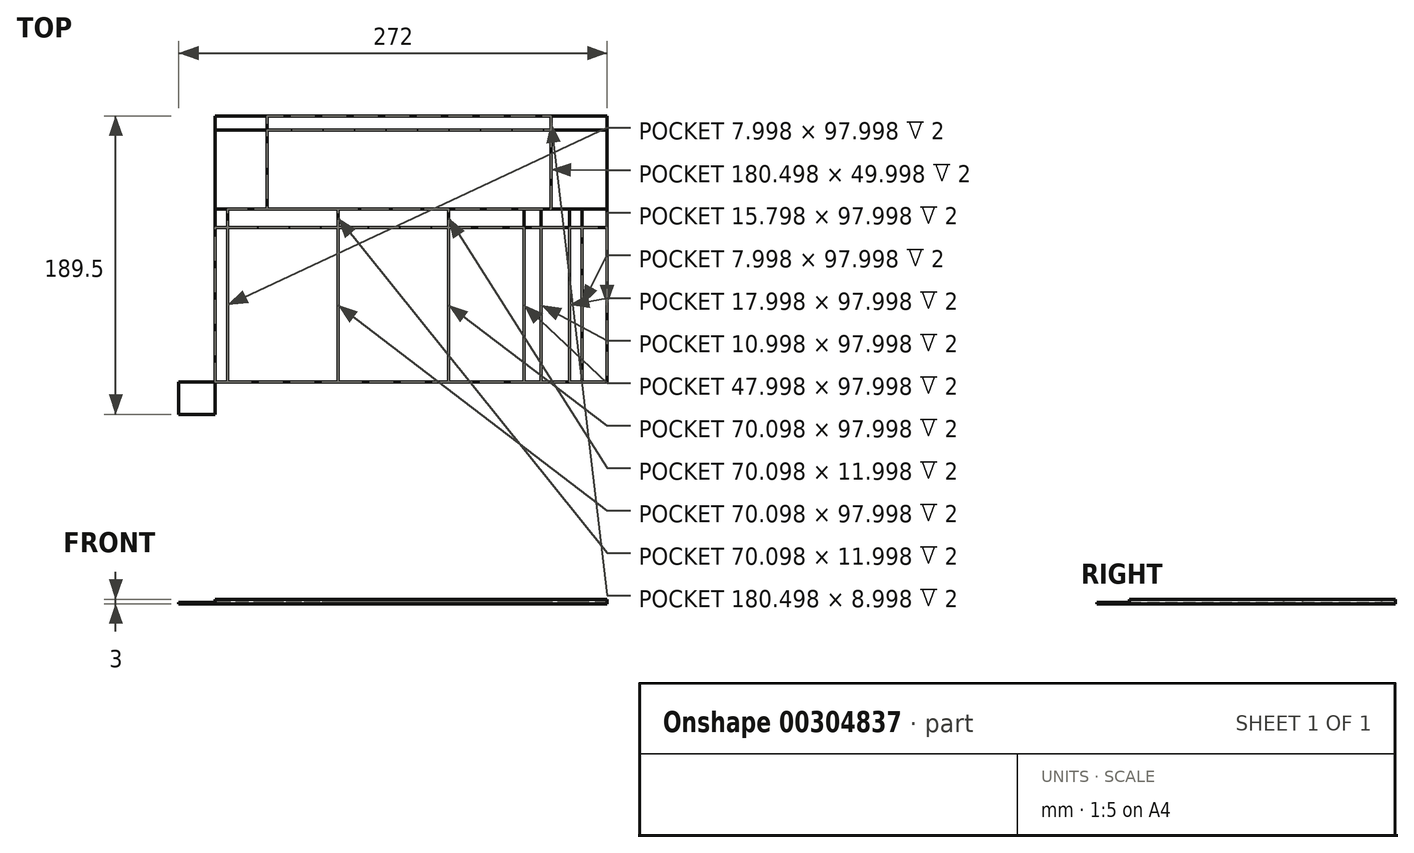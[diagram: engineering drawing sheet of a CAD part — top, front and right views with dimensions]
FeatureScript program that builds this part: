
annotation { "Feature Type Name" : "Feature", "Feature Type Description" : "" }
export const myFeature = defineFeature(function(context is Context, id is Id, definition is map)
    precondition{}
    {
        {
            var Q0;
            Q0=qCreatedBy(makeId("Top.planeOp"),FACE);
            var sketch = newSketch(context, id + "F0", { "sketchPlane" : qUnion([Q0])});
            skLineSegment(sketch, "E0.bottom", {"start": v(0, 0) * mm, "end": v(290, 0) * mm, "construction": true});
            skLineSegment(sketch, "E0.top", {"start": v(0, 210) * mm, "end": v(290, 210) * mm, "construction": true});
            skLineSegment(sketch, "E0.left", {"start": v(0, 0) * mm, "end": v(0, 210) * mm, "construction": true});
            skLineSegment(sketch, "E0.right", {"start": v(290, 0) * mm, "end": v(290, 210) * mm, "construction": true});
            skLineSegment(sketch, "E1.0", {"start": v(20.5, 189.5) * mm, "end": v(269.5, 189.5) * mm});
            skLineSegment(sketch, "E1.1", {"start": v(20.5, 20.5) * mm, "end": v(20.5, 189.5) * mm});
            skLineSegment(sketch, "E1.2", {"start": v(20.5, 20.5) * mm, "end": v(269.5, 20.5) * mm});
            skLineSegment(sketch, "E1.3", {"start": v(269.5, 20.5) * mm, "end": v(269.5, 189.5) * mm});
            skSolve(sketch);
        }
        {
            var Q0;
            Q0=qCreatedBy(makeId("Top.planeOp"),FACE);
            var sketch = newSketch(context, id + "F1", { "sketchPlane" : qUnion([Q0])});
            skLineSegment(sketch, "E2.bottom", {"start": v(20.5, 189.5) * mm, "end": v(53.5, 189.5) * mm});
            skLineSegment(sketch, "E2.top", {"start": v(20.5, 180.5) * mm, "end": v(53.5, 180.5) * mm});
            skLineSegment(sketch, "E2.left", {"start": v(20.5, 189.5) * mm, "end": v(20.5, 180.5) * mm});
            skLineSegment(sketch, "E2.right", {"start": v(53.5, 189.5) * mm, "end": v(53.5, 180.5) * mm});
            skLineSegment(sketch, "E3.bottom", {"start": v(53.5, 189.5) * mm, "end": v(234, 189.5) * mm});
            skLineSegment(sketch, "E3.top", {"start": v(53.5, 180.5) * mm, "end": v(234, 180.5) * mm});
            skLineSegment(sketch, "E3.right", {"start": v(234, 189.5) * mm, "end": v(234, 180.5) * mm});
            skLineSegment(sketch, "E4.bottom", {"start": v(234, 189.5) * mm, "end": v(269.5, 189.5) * mm});
            skLineSegment(sketch, "E4.top", {"start": v(234, 180.5) * mm, "end": v(269.5, 180.5) * mm});
            skLineSegment(sketch, "E4.right", {"start": v(269.5, 189.5) * mm, "end": v(269.5, 180.5) * mm});
            skLineSegment(sketch, "E5.top", {"start": v(20.5, 130.5) * mm, "end": v(53.5, 130.5) * mm});
            skLineSegment(sketch, "E5.left", {"start": v(20.5, 180.5) * mm, "end": v(20.5, 130.5) * mm});
            skLineSegment(sketch, "E5.right", {"start": v(53.5, 180.5) * mm, "end": v(53.5, 130.5) * mm});
            skLineSegment(sketch, "E6.top", {"start": v(53.5, 130.5) * mm, "end": v(234, 130.5) * mm});
            skLineSegment(sketch, "E6.right", {"start": v(234, 180.5) * mm, "end": v(234, 130.5) * mm});
            skLineSegment(sketch, "E7.top", {"start": v(234, 130.5) * mm, "end": v(269.5, 130.5) * mm});
            skLineSegment(sketch, "E7.right", {"start": v(269.5, 180.5) * mm, "end": v(269.5, 130.5) * mm});
            skLineSegment(sketch, "E8.bottom", {"start": v(20.5, 180.5) * mm, "end": v(269.5, 180.5) * mm});
            skLineSegment(sketch, "E8.top", {"start": v(20.5, 189.5) * mm, "end": v(269.5, 189.5) * mm});
            skLineSegment(sketch, "E8.left", {"start": v(20.5, 180.5) * mm, "end": v(20.5, 189.5) * mm});
            skLineSegment(sketch, "E8.right", {"start": v(269.5, 180.5) * mm, "end": v(269.5, 189.5) * mm});
            skLineSegment(sketch, "E9.bottom", {"start": v(20.5, 130.5) * mm, "end": v(28.5, 130.5) * mm});
            skLineSegment(sketch, "E9.top", {"start": v(20.5, 118.5) * mm, "end": v(28.5, 118.5) * mm, "construction": true});
            skLineSegment(sketch, "E9.left", {"start": v(20.5, 130.5) * mm, "end": v(20.5, 118.5) * mm});
            skLineSegment(sketch, "E9.right", {"start": v(28.5, 130.5) * mm, "end": v(28.5, 118.5) * mm, "construction": true});
            skLineSegment(sketch, "E10.2", {"start": v(20.5, 118.5) * mm, "end": v(28.5, 118.5) * mm});
            skLineSegment(sketch, "E10.3", {"start": v(28.5, 130.5) * mm, "end": v(28.5, 118.5) * mm});
            skLineSegment(sketch, "E11.top", {"start": v(20.5, 20.5) * mm, "end": v(28.5, 20.5) * mm});
            skLineSegment(sketch, "E11.left", {"start": v(20.5, 118.5) * mm, "end": v(20.5, 20.5) * mm});
            skLineSegment(sketch, "E11.right", {"start": v(28.5, 118.5) * mm, "end": v(28.5, 20.5) * mm, "construction": true});
            skLineSegment(sketch, "E12.3", {"start": v(28.5, 118.5) * mm, "end": v(28.5, 20.5) * mm});
            skLineSegment(sketch, "E13.bottom", {"start": v(28.5, 130.5) * mm, "end": v(98.6, 130.5) * mm});
            skLineSegment(sketch, "E13.top", {"start": v(28.5, 118.5) * mm, "end": v(98.6, 118.5) * mm, "construction": true});
            skLineSegment(sketch, "E13.right", {"start": v(98.6, 130.5) * mm, "end": v(98.6, 118.5) * mm, "construction": true});
            skLineSegment(sketch, "E14.2", {"start": v(28.5, 118.5) * mm, "end": v(98.6, 118.5) * mm});
            skLineSegment(sketch, "E14.3", {"start": v(98.6, 130.5) * mm, "end": v(98.6, 118.5) * mm});
            skLineSegment(sketch, "E15.top", {"start": v(28.5, 20.5) * mm, "end": v(98.6, 20.5) * mm});
            skLineSegment(sketch, "E15.right", {"start": v(98.6, 118.5) * mm, "end": v(98.6, 20.5) * mm, "construction": true});
            skLineSegment(sketch, "E16.3", {"start": v(98.6, 118.5) * mm, "end": v(98.6, 20.5) * mm});
            skLineSegment(sketch, "E17.bottom", {"start": v(98.6, 130.5) * mm, "end": v(168.7, 130.5) * mm, "construction": true});
            skLineSegment(sketch, "E17.top", {"start": v(98.6, 118.5) * mm, "end": v(168.7, 118.5) * mm, "construction": true});
            skLineSegment(sketch, "E17.right", {"start": v(168.7, 130.5) * mm, "end": v(168.7, 118.5) * mm, "construction": true});
            skLineSegment(sketch, "E18.0", {"start": v(98.6, 130.5) * mm, "end": v(168.7, 130.5) * mm});
            skLineSegment(sketch, "E18.2", {"start": v(98.6, 118.5) * mm, "end": v(168.7, 118.5) * mm});
            skLineSegment(sketch, "E18.3", {"start": v(168.7, 130.5) * mm, "end": v(168.7, 118.5) * mm});
            skLineSegment(sketch, "E19.top", {"start": v(98.6, 20.5) * mm, "end": v(168.7, 20.5) * mm, "construction": true});
            skLineSegment(sketch, "E19.right", {"start": v(168.7, 118.5) * mm, "end": v(168.7, 20.5) * mm, "construction": true});
            skLineSegment(sketch, "E20.2", {"start": v(98.6, 20.5) * mm, "end": v(168.7, 20.5) * mm});
            skLineSegment(sketch, "E20.3", {"start": v(168.7, 118.5) * mm, "end": v(168.7, 20.5) * mm});
            skLineSegment(sketch, "E21.bottom", {"start": v(168.7, 130.5) * mm, "end": v(216.7, 130.5) * mm, "construction": true});
            skLineSegment(sketch, "E21.top", {"start": v(168.7, 118.5) * mm, "end": v(216.7, 118.5) * mm, "construction": true});
            skLineSegment(sketch, "E21.right", {"start": v(216.7, 130.5) * mm, "end": v(216.7, 118.5) * mm, "construction": true});
            skLineSegment(sketch, "E22.0", {"start": v(168.7, 130.5) * mm, "end": v(216.7, 130.5) * mm});
            skLineSegment(sketch, "E22.2", {"start": v(168.7, 118.5) * mm, "end": v(216.7, 118.5) * mm});
            skLineSegment(sketch, "E22.3", {"start": v(216.7, 130.5) * mm, "end": v(216.7, 118.5) * mm});
            skLineSegment(sketch, "E23.top", {"start": v(168.7, 20.5) * mm, "end": v(216.7, 20.5) * mm, "construction": true});
            skLineSegment(sketch, "E23.right", {"start": v(216.7, 118.5) * mm, "end": v(216.7, 20.5) * mm, "construction": true});
            skLineSegment(sketch, "E24.2", {"start": v(168.7, 20.5) * mm, "end": v(216.7, 20.5) * mm});
            skLineSegment(sketch, "E24.3", {"start": v(216.7, 118.5) * mm, "end": v(216.7, 20.5) * mm});
            skLineSegment(sketch, "E25.bottom", {"start": v(216.7, 130.5) * mm, "end": v(224.7, 130.5) * mm, "construction": true});
            skLineSegment(sketch, "E25.top", {"start": v(216.7, 118.5) * mm, "end": v(224.7, 118.5) * mm, "construction": true});
            skLineSegment(sketch, "E26.0", {"start": v(216.7, 130.5) * mm, "end": v(227.7, 130.5) * mm});
            skLineSegment(sketch, "E26.2", {"start": v(216.7, 118.5) * mm, "end": v(227.7, 118.5) * mm});
            skLineSegment(sketch, "E26.3", {"start": v(227.7, 130.5) * mm, "end": v(227.7, 118.5) * mm});
            skLineSegment(sketch, "E27.bottom", {"start": v(216.7, 118.5) * mm, "end": v(227.7, 118.5) * mm, "construction": true});
            skLineSegment(sketch, "E27.top", {"start": v(216.7, 20.5) * mm, "end": v(227.7, 20.5) * mm, "construction": true});
            skLineSegment(sketch, "E27.right", {"start": v(227.7, 118.5) * mm, "end": v(227.7, 20.5) * mm, "construction": true});
            skLineSegment(sketch, "E28.2", {"start": v(216.7, 20.5) * mm, "end": v(227.7, 20.5) * mm});
            skLineSegment(sketch, "E28.3", {"start": v(227.7, 118.5) * mm, "end": v(227.7, 20.5) * mm});
            skLineSegment(sketch, "E29.bottom", {"start": v(227.7, 130.5) * mm, "end": v(235.7, 130.5) * mm, "construction": true});
            skLineSegment(sketch, "E29.left", {"start": v(227.7, 130.5) * mm, "end": v(227.7, 118.5) * mm, "construction": true});
            skLineSegment(sketch, "E30.0", {"start": v(227.7, 130.5) * mm, "end": v(245.7, 130.5) * mm});
            skLineSegment(sketch, "E30.2", {"start": v(227.7, 118.5) * mm, "end": v(245.7, 118.5) * mm});
            skLineSegment(sketch, "E30.3", {"start": v(245.7, 130.5) * mm, "end": v(245.7, 118.5) * mm});
            skLineSegment(sketch, "E31.bottom", {"start": v(227.7, 118.5) * mm, "end": v(245.7, 118.5) * mm, "construction": true});
            skLineSegment(sketch, "E31.top", {"start": v(227.7, 20.5) * mm, "end": v(245.7, 20.5) * mm, "construction": true});
            skLineSegment(sketch, "E31.right", {"start": v(245.7, 118.5) * mm, "end": v(245.7, 20.5) * mm, "construction": true});
            skLineSegment(sketch, "E32.2", {"start": v(227.7, 20.5) * mm, "end": v(245.7, 20.5) * mm});
            skLineSegment(sketch, "E32.3", {"start": v(245.7, 118.5) * mm, "end": v(245.7, 20.5) * mm});
            skLineSegment(sketch, "E33.bottom", {"start": v(482.93, -80.3) * mm, "end": v(490.93, -80.3) * mm, "construction": true});
            skLineSegment(sketch, "E33.top", {"start": v(482.93, -92.3) * mm, "end": v(490.93, -92.3) * mm, "construction": true});
            skLineSegment(sketch, "E33.left", {"start": v(482.93, -80.3) * mm, "end": v(482.93, -92.3) * mm, "construction": true});
            skLineSegment(sketch, "E33.right", {"start": v(490.93, -80.3) * mm, "end": v(490.93, -92.3) * mm, "construction": true});
            skLineSegment(sketch, "E34.0", {"start": v(482.93, -80.3) * mm, "end": v(490.93, -80.3) * mm});
            skLineSegment(sketch, "E34.1", {"start": v(482.93, -80.3) * mm, "end": v(482.93, -92.3) * mm});
            skLineSegment(sketch, "E34.2", {"start": v(482.93, -92.3) * mm, "end": v(490.93, -92.3) * mm});
            skLineSegment(sketch, "E34.3", {"start": v(490.93, -80.3) * mm, "end": v(490.93, -92.3) * mm});
            skLineSegment(sketch, "E35.top", {"start": v(482.93, -190.3) * mm, "end": v(490.93, -190.3) * mm, "construction": true});
            skLineSegment(sketch, "E35.left", {"start": v(482.93, -92.3) * mm, "end": v(482.93, -190.3) * mm, "construction": true});
            skLineSegment(sketch, "E35.right", {"start": v(490.93, -92.3) * mm, "end": v(490.93, -190.3) * mm, "construction": true});
            skLineSegment(sketch, "E36.1", {"start": v(482.93, -92.3) * mm, "end": v(482.93, -190.3) * mm});
            skLineSegment(sketch, "E36.2", {"start": v(482.93, -190.3) * mm, "end": v(490.93, -190.3) * mm});
            skLineSegment(sketch, "E36.3", {"start": v(490.93, -92.3) * mm, "end": v(490.93, -190.3) * mm});
            skLineSegment(sketch, "E37.bottom", {"start": v(245.7, 130.5) * mm, "end": v(253.7, 130.5) * mm, "construction": true});
            skLineSegment(sketch, "E37.top", {"start": v(245.7, 118.5) * mm, "end": v(253.7, 118.5) * mm, "construction": true});
            skLineSegment(sketch, "E37.left", {"start": v(245.7, 130.5) * mm, "end": v(245.7, 118.5) * mm, "construction": true});
            skLineSegment(sketch, "E37.right", {"start": v(253.7, 130.5) * mm, "end": v(253.7, 118.5) * mm, "construction": true});
            skLineSegment(sketch, "E38.0", {"start": v(245.7, 130.5) * mm, "end": v(253.7, 130.5) * mm});
            skLineSegment(sketch, "E38.2", {"start": v(245.7, 118.5) * mm, "end": v(253.7, 118.5) * mm});
            skLineSegment(sketch, "E38.3", {"start": v(253.7, 130.5) * mm, "end": v(253.7, 118.5) * mm});
            skLineSegment(sketch, "E39.top", {"start": v(245.7, 20.5) * mm, "end": v(253.7, 20.5) * mm, "construction": true});
            skLineSegment(sketch, "E39.right", {"start": v(253.7, 118.5) * mm, "end": v(253.7, 20.5) * mm, "construction": true});
            skLineSegment(sketch, "E40.2", {"start": v(245.7, 20.5) * mm, "end": v(253.7, 20.5) * mm});
            skLineSegment(sketch, "E40.3", {"start": v(253.7, 118.5) * mm, "end": v(253.7, 20.5) * mm});
            skLineSegment(sketch, "E41.bottom", {"start": v(253.7, 130.5) * mm, "end": v(269.5, 130.5) * mm, "construction": true});
            skLineSegment(sketch, "E41.top", {"start": v(253.7, 118.5) * mm, "end": v(269.5, 118.5) * mm, "construction": true});
            skLineSegment(sketch, "E41.right", {"start": v(269.5, 130.5) * mm, "end": v(269.5, 118.5) * mm, "construction": true});
            skLineSegment(sketch, "E42.0", {"start": v(253.7, 130.5) * mm, "end": v(269.5, 130.5) * mm});
            skLineSegment(sketch, "E42.2", {"start": v(253.7, 118.5) * mm, "end": v(269.5, 118.5) * mm});
            skLineSegment(sketch, "E42.3", {"start": v(269.5, 130.5) * mm, "end": v(269.5, 118.5) * mm});
            skLineSegment(sketch, "E43.top", {"start": v(253.7, 20.5) * mm, "end": v(269.5, 20.5) * mm, "construction": true});
            skLineSegment(sketch, "E43.right", {"start": v(269.5, 118.5) * mm, "end": v(269.5, 20.5) * mm, "construction": true});
            skLineSegment(sketch, "E44.2", {"start": v(253.7, 20.5) * mm, "end": v(269.5, 20.5) * mm});
            skLineSegment(sketch, "E44.3", {"start": v(269.5, 118.5) * mm, "end": v(269.5, 20.5) * mm});
            skLineSegment(sketch, "E45.top", {"start": v(20.5, 20.5) * mm, "end": v(269.5, 20.5) * mm});
            skLineSegment(sketch, "E45.left", {"start": v(20.5, 189.5) * mm, "end": v(20.5, 20.5) * mm});
            skLineSegment(sketch, "E45.right", {"start": v(269.5, 189.5) * mm, "end": v(269.5, 20.5) * mm});
            skLineSegment(sketch, "E46.bottom", {"start": v(20.5, 20.5) * mm, "end": v(-2.5, 20.5) * mm});
            skLineSegment(sketch, "E46.top", {"start": v(20.5, 0) * mm, "end": v(-2.5, 0) * mm});
            skLineSegment(sketch, "E46.left", {"start": v(20.5, 20.5) * mm, "end": v(20.5, 0) * mm});
            skLineSegment(sketch, "E46.right", {"start": v(-2.5, 20.5) * mm, "end": v(-2.5, 0) * mm});
            skSolve(sketch);
        }
        {
            var Q0;
            Q0=makeQuery(id+"F0.imprint","IMPRINT",FACE,{"disambiguationData":[TD([[makeQuery(id+"F0.imprint","IMPRINT",EDGE,{"derivedFrom":sQuery(id+"F0.wireOp",EDGE,"E1.0")}),-1.0]])]});
            extrude(context, id + "F2", {"entities" : qUnion([Q0]), "depth" : 1 * mm});
        }
        {
            var Q0;
            Q0=makeQuery(id+"F1.imprint","IMPRINT",FACE,{"disambiguationData":[TD([[makeQuery(id+"F1.imprint","IMPRINT",EDGE,{"derivedFrom":sQuery(id+"F1.wireOp",EDGE,"E2.top")}),1.0]])]});
            var Q1;
            {var subQ3=sQuery(id+"F1.wireOp",EDGE,"E6.top");Q1=makeQuery(id+"F1.imprint","IMPRINT",FACE,{"disambiguationData":[TD([[makeQuery(id+"F1.imprint","IMPRINT",EDGE,{"derivedFrom":subQ3}),1.0]])]});}
            var Q2;
            {var subQ3=sQuery(id+"F1.wireOp",EDGE,"E6.top");Q2=makeQuery(id+"F1.imprint","IMPRINT",FACE,{"disambiguationData":[TD([[makeQuery(id+"F1.imprint","IMPRINT",EDGE,{"derivedFrom":subQ3}),-1.0]])]});}
            var Q3;
            {var subQ1=sQuery(id+"F1.wireOp",EDGE,"E10.2");Q3=makeQuery(id+"F1.imprint","IMPRINT",FACE,{"disambiguationData":[TD([[makeQuery(id+"F1.imprint","IMPRINT",EDGE,{"derivedFrom":subQ1}),-1.0]])]});}
            var Q4;
            {var subQ0=sQuery(id+"F1.wireOp",EDGE,"E9.bottom");Q4=makeQuery(id+"F1.imprint","IMPRINT",FACE,{"disambiguationData":[TD([[makeQuery(id+"F1.imprint","IMPRINT",EDGE,{"derivedFrom":subQ0}),-1.0]])]});}
            var Q5;
            {var subQ0=sQuery(id+"F1.wireOp",EDGE,"E2.right");Q5=makeQuery(id+"F1.imprint","IMPRINT",FACE,{"disambiguationData":[TD([[makeQuery(id+"F1.imprint","IMPRINT",EDGE,{"derivedFrom":subQ0}),1.0]])]});}
            var Q6;
            Q6=makeQuery(id+"F1.imprint","IMPRINT",FACE,{"disambiguationData":[TD([[makeQuery(id+"F1.imprint","IMPRINT",EDGE,{"derivedFrom":sQuery(id+"F1.wireOp",EDGE,"E2.bottom")}),1.0]])]});
            var Q7;
            {var subQ1=sQuery(id+"F1.wireOp",EDGE,"E3.right");Q7=makeQuery(id+"F1.imprint","IMPRINT",FACE,{"disambiguationData":[TD([[makeQuery(id+"F1.imprint","IMPRINT",EDGE,{"derivedFrom":subQ1}),1.0]])]});}
            var Q8;
            {var subQ1=sQuery(id+"F1.wireOp",EDGE,"E7.top");Q8=makeQuery(id+"F1.imprint","IMPRINT",FACE,{"disambiguationData":[TD([[makeQuery(id+"F1.imprint","IMPRINT",EDGE,{"derivedFrom":subQ1}),1.0]])]});}
            extrude(context, id + "F3", {"entities" : qUnion([Q0, Q1, Q2, Q3, Q4, Q5, Q6, Q7, Q8]), "operationType" : NewBodyOperationType.ADD, "depth" : 3 * mm});
        }
        {
            var Q0;
            Q0=makeQuery(id+"F1.imprint","IMPRINT",FACE,{"disambiguationData":[TD([[makeQuery(id+"F1.imprint","IMPRINT",EDGE,{"derivedFrom":sQuery(id+"F1.wireOp",EDGE,"E46.bottom")}),1.0]])]});
            extrude(context, id + "F4", {"entities" : qUnion([Q0]), "depth" : 1 * mm});
        }
    });
